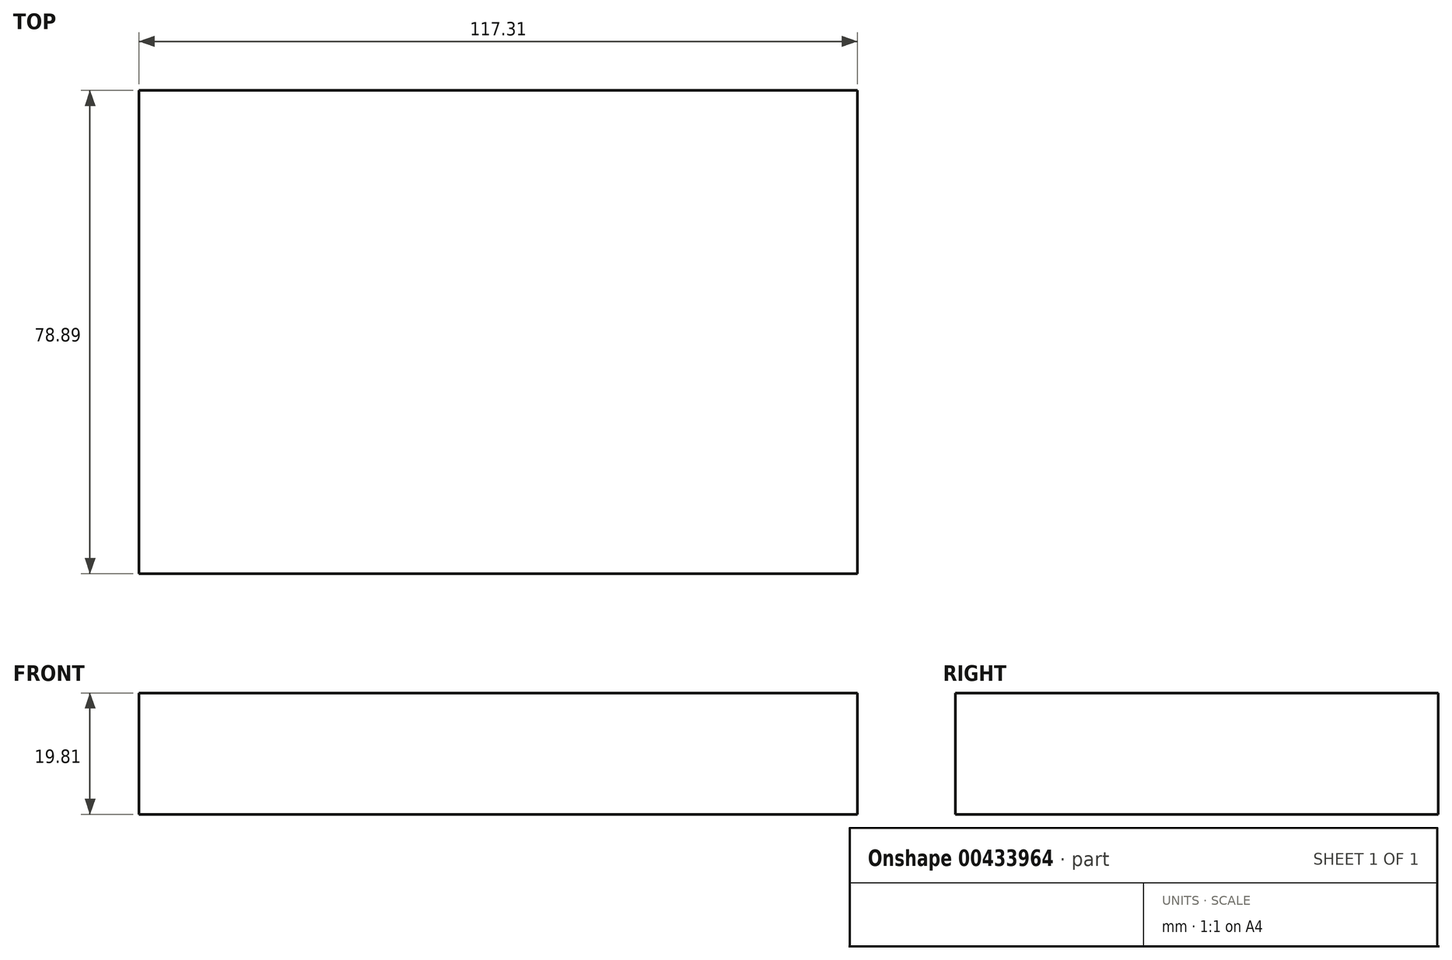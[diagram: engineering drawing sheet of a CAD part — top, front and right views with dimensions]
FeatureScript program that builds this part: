
annotation { "Feature Type Name" : "Feature", "Feature Type Description" : "" }
export const myFeature = defineFeature(function(context is Context, id is Id, definition is map)
    precondition{}
    {
        {
            var Q0;
            Q0=qCreatedBy(makeId("Top.planeOp"),FACE);
            var sketch = newSketch(context, id + "F0", { "sketchPlane" : qUnion([Q0])});
            skLineSegment(sketch, "E0.bottom", {"start": v(-59.87, 43.27) * mm, "end": v(57.44, 43.27) * mm});
            skLineSegment(sketch, "E0.top", {"start": v(-59.87, -35.62) * mm, "end": v(57.44, -35.62) * mm});
            skLineSegment(sketch, "E0.left", {"start": v(-59.87, 43.27) * mm, "end": v(-59.87, -35.62) * mm});
            skLineSegment(sketch, "E0.right", {"start": v(57.44, 43.27) * mm, "end": v(57.44, -35.62) * mm});
            skSolve(sketch);
        }
        {
            var Q0;
            Q0 = qSketchRegion(id + "F0", true);
            extrude(context, id + "F1", {"entities" : qUnion([Q0]), "depth" : 19.8 * mm});
        }
    });
